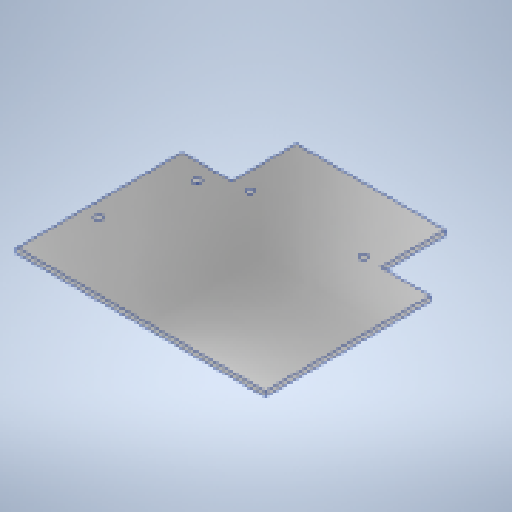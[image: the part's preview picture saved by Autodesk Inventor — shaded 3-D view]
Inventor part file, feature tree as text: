
AUTODESK INVENTOR PART (.ipt)
format: ipt  version: 2023 (Build 270158000, 158)  size: 201,216 bytes
history: native  units: mm
features: sketch x8, extrude x7, projected_geometry x3, other x2, reference x1
ambient origin geometry x8: Origin, YZ Plane, XZ Plane, XY Plane, X Axis, Y Axis, Z Axis, Center Point
bodies: Solid1 (feature_tree)
feature tree (21):
  extrude  "Extrusion1"  Depth=100.0mm
  extrude  "Extrusion2"  Depth=20.0mm
  extrude  "Wyciągnięcie proste3"  Depth=10.0mm
  extrude  "Wyciągnięcie proste4"  Depth=20.0mm
  extrude  "Wyciągnięcie proste5"  Depth=2.0mm TaperAngle=0.0deg
  extrude  "Wyciągnięcie proste6"  Depth=10.0mm
  extrude  "Wyciągnięcie proste7"  Depth=2.0mm TaperAngle=0.0deg
  sketch  "Szkic8"
  sketch  "Sketch1"  dims[d0=100.0mm d1=100.0mm]
  sketch  "Sketch2"  dims[d2=5.0mm d3=20.0mm d4=31.0mm d5=20.0mm d6=2.0mm d7=0.0mm d8=5.0mm d9=2.0mm d10=0.0mm d11=0.0mm d12=0.0mm d13=10.0mm d14=0.0mm d15=0.0mm d16=0.0mm d17=2.5mm d18=0.0mm d19=0.0mm d20=0.0mm d21=25.6mm d22=28.0mm]
  reference  "Reference1"
  sketch  "Szkic3"
  sketch  "Szkic4"
  projected_geometry  "Pętla rzutowana1"
  sketch  "Szkic5"
  sketch  "Szkic6"
  projected_geometry  "Pętla rzutowana2"
  sketch  "Szkic7"
  projected_geometry  "Pętla rzutowana3"
  other  "Assembly2"
  other  "dach]:1"
